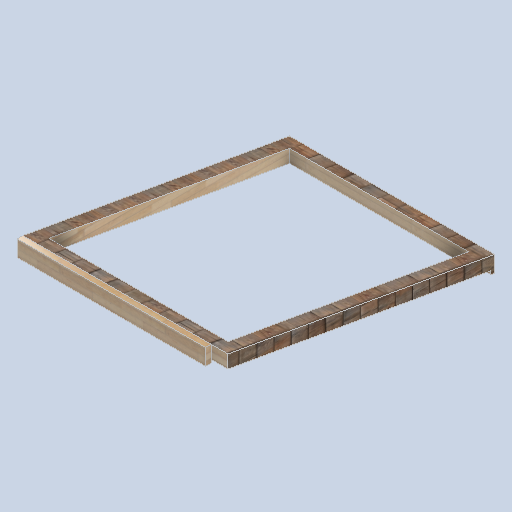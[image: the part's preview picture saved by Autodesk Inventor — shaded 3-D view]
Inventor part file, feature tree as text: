
AUTODESK INVENTOR PART (.ipt)
format: ipt  version: 2024.2 (Build 282272000, 272)  size: 183,808 bytes
history: native  units: in
note: dims shown in document units (in); Inventor stores cm internally (conversion verified against a paired STEP export)
features: sketch x7, plane x5, other x3
ambient origin geometry x8: Origin, YZ Plane, XZ Plane, XY Plane, X Axis, Y Axis, Z Axis, Center Point
bodies: Solid1 (feature_tree)
feature tree (15):
  other  "eave_frame_02.ipt"
  other  "Solid1::eave_frame_02.ipt"
  other  "TaggingFeature1"
  sketch  "Sketch3"  dims[d0=0.3937in]
  sketch  "Sketch4"
  sketch  "Sketch5"
  sketch  "Sketch6"
  sketch  "Sketch7"
  sketch  "Sketch8"
  sketch  "Sketch9"
  plane  "Work Plane1"
  plane  "Work Plane2"
  plane  "Work Plane3"
  plane  "Work Plane4"
  plane  "Work Plane5"
